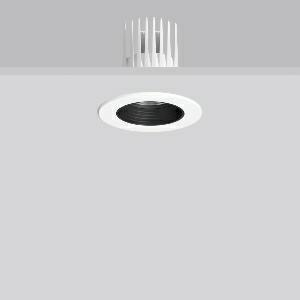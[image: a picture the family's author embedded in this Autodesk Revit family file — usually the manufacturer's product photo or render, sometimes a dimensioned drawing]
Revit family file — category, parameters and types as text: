
# Revit family: heledon_mini_e_901746_002_3_96d3
name_source: partatom
category: Lighting Fixtures
units: mm (PartAtom-declared; Revit-internal decimal feet)

## family parameters
Cut with Voids When Loaded = No
Host = Face
Light Source = No
Part Type = Normal
Room Calculation Point = No
Round Connector Dimension = Use Diameter
Shared = No

## types (1)
- HELEDON mini E (1 x LED Modul 935, 2300 lm, 3500)
    Apparent Load = 20 VA
    Approval mark = CE
    CIE Flux Codes = 80 99 100 100 100
    Color Rendering = 92
    Color Temperature = 3500
    Default Elevation = 1800 mm
    Description = Series: HELEDON mini
Round recessed downlight. Housing: die-cast aluminium, powder-coated. Black plastic ring and recessed LED to prevent glare from the side. Optical assembly with lens made of plastic (polycarbonate) for the best homogeneous light distribution - can be changed without tools. Best colour rendering index Ra>90. Suitable for Recessed ceiling mounting. Installation without tools thanks to spring fastening system. Including separate LED converter with connecting cable 600 mm.High quality converter without flickering and stroboscopic effect. Through-wiring box (5 pole) available as accessory. The following accessories can be mounted without use of tools: interchangeable lenses, decorative glasses, honeycomb louvre, clear and frosted diffusers, white interchangeable plastic ring. 
Colour: traffic white, matt (RAL 9016)
Diameter: 124 mm
Height: 3 mm
Cut-out diameter: 114 mm
Recess height: 170 mm
Luminaire: recess height: 120 mm
Lamp: LED
Socket: without socket
Colour temperature: 3500K
Colour rendering index (CRI): 92
System power: 20 W
Rated luminous flux: 2300 lm
Luminous efficiency: 115 lm/W
Control gear: Regulated power supply
Protection class: II
Type of protection: IP 20
    Height = 0 mm  [stored 0 ft]
    Lamp = 1 x LED Modul 935
    Lamp Light Flux = 2300 lm
    Lamp count = 1
    Length = 124 mm  [stored 0.406824 ft]
    Lifetime = 50000 h
    Luminous efficacy = 115 lm/W
    Manufacturer = RZB
    ModVariant = No
    Model = 901746.002.3
    Mounting Place = Ceiling
    Mounting Type = Recessed
    Number of Poles = 1
    OnlyDefault = Yes
    Power Factor = 1
    Product Name = HELEDON mini E
    Product group = Recessed downlights
    ProductGroupID = 402
    Protection Class = Protection class II
    Protection Degree = IP 20
    RLX_Detail_Level = 1
    RLX_Emergency_Light_Flux = 0 lm
    RLX_Emergency_Type = 0
    RLX_Emergency_Type_DB = No
    RlxData = <blob elided: 123505 chars, md5=c7e00dd8>
    Socket = socket
    Standby Power = 0 W
    System Light Flux = 2300 lm
    System Power = 20 W
    Type Comments = Product without accessories
    Type Image = 901656.002.jpg
    URL = http://relux.com
    VarID = ---
    Voltage = 230 V
    Voltage Range = 220-240 V
    Weight = 0.00 kg
    Width = 0 mm  [stored 0 ft]

note: [stored X ft] marks values corroborated as IEEE doubles in the binary element streams (Revit-internal decimal feet)

## geometry (parser evidence)
native form markers: Blend x4, Sweep x11
no freeform markers — native parametric forms only
